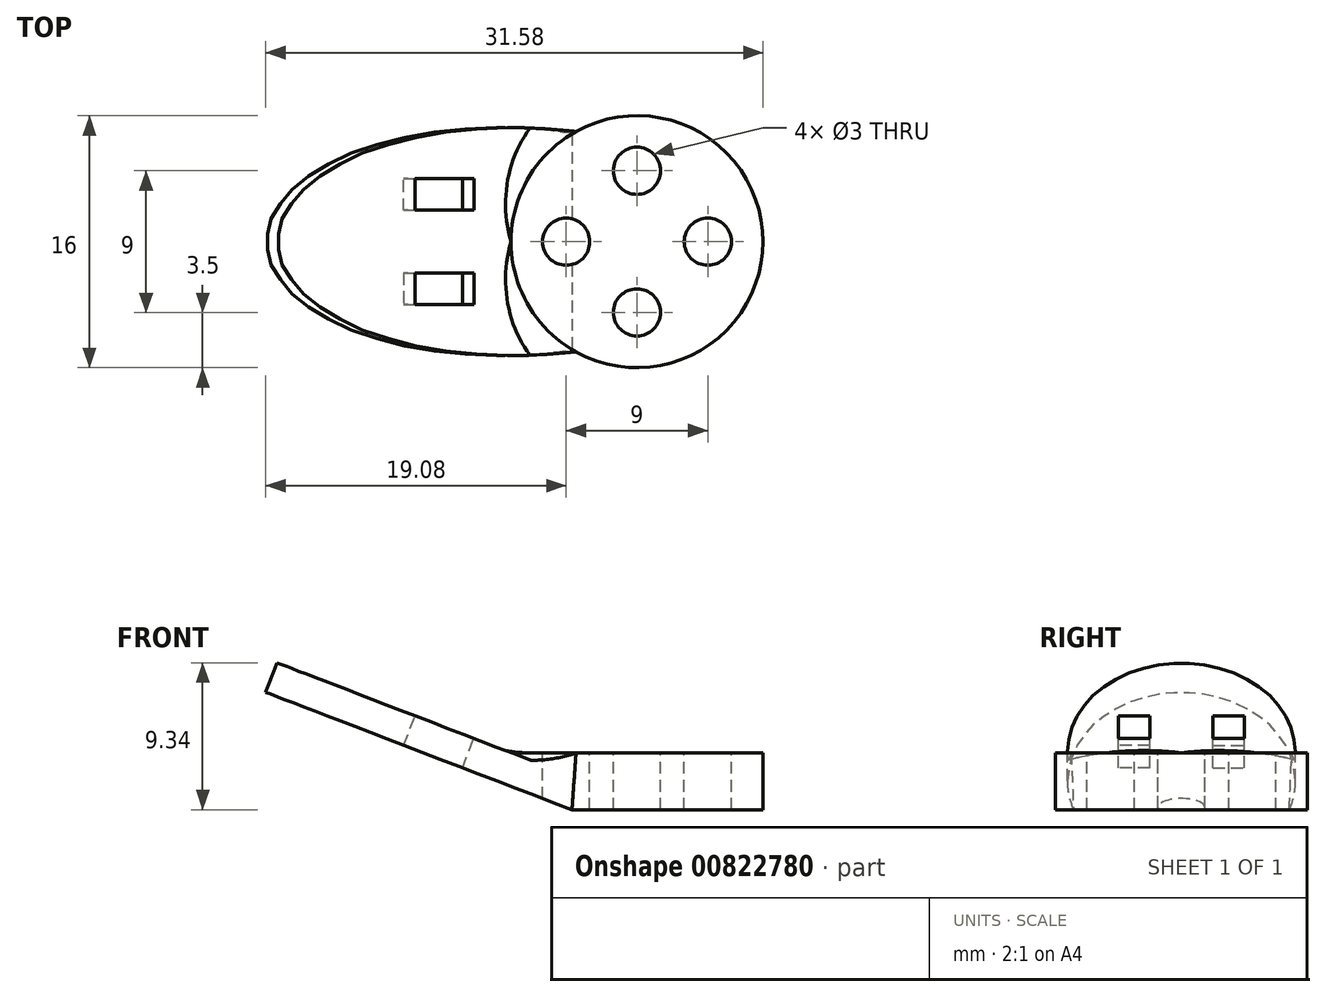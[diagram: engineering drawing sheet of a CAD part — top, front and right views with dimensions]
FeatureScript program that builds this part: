
annotation { "Feature Type Name" : "Feature", "Feature Type Description" : "" }
export const myFeature = defineFeature(function(context is Context, id is Id, definition is map)
    precondition{}
    {
        {
            var Q0;
            Q0=qCreatedBy(makeId("Top.planeOp"),FACE);
            var sketch = newSketch(context, id + "F0", { "sketchPlane" : qUnion([Q0])});
            skCircle(sketch, "E0", {"center": v(0, 0) * mm, "radius": 8 * mm});
            skPoint(sketch, "E1", {"position": v(-8, 0) * mm});
            skSolve(sketch);
        }
        {
            var Q0;
            Q0=qCreatedBy(makeId("Front.planeOp"),FACE);
            var sketch = newSketch(context, id + "F1", { "sketchPlane" : qUnion([Q0])});
            skLineSegment(sketch, "E2", {"start": v(0, 0) * mm, "end": v(6.14, 15.98) * mm});
            skSolve(sketch);
        }
        {
            var Q0;
            Q0=sQuery(id+"F0.wireOp",VERTEX,"E1");
            var Q1;
            Q1=sQuery(id+"F1.wireOp",EDGE,"E2");
            cPlane(context, id + "F2", {"entities" : qUnion([Q0, Q1]), "cplaneType" : CPlaneType.LINE_POINT, "offset" : 25 * mm, "width" : 150 * mm, "height" : 150 * mm});
        }
        {
            var Q0;
            Q0=qCreatedBy(id+"F2.planeOp",FACE);
            var sketch = newSketch(context, id + "F3", { "sketchPlane" : qUnion([Q0])});
            skEllipse(sketch, "E3", {"center": v(-7.69, 0) * mm, "majorRadius": 15.7 * mm, "minorRadius": 7.25 * mm, "majorAxis": v(-1, 0)});
            skSolve(sketch);
        }
        {
            var Q0;
            Q0=makeQuery(id+"F3.imprint","IMPRINT",FACE,{"disambiguationData":[TD([[makeQuery(id+"F3.imprint","IMPRINT",EDGE,{"derivedFrom":sQuery(id+"F3.wireOp",EDGE,"E3")}),1.0]])]});
            extrude(context, id + "F4", {"entities" : qUnion([Q0]), "oppositeDirection" : true, "depth" : 2 * mm, "offsetDistance" : 25 * mm});
        }
        {
            var Q0;
            Q0=makeQuery(id+"F0.imprint","IMPRINT",FACE,{"disambiguationData":[TD([[makeQuery(id+"F0.imprint","IMPRINT",EDGE,{"derivedFrom":sQuery(id+"F0.wireOp",EDGE,"E0")}),1.0]])]});
            var Q1;
            Q1=makeQuery(id+"F4.opExtrude","CAP_FACE",FACE,{"disambiguationData":[OSD([sQuery(id+"F3.wireOp",EDGE,"E3")])],"isStart":false});
            extrude(context, id + "F5", {"entities" : qUnion([Q0]), "operationType" : NewBodyOperationType.ADD, "endBound" : BoundingType.UP_TO_SURFACE, "oppositeDirection" : true, "depth" : 25 * mm, "endBoundEntityFace" : qUnion([Q1]), "offsetDistance" : 25 * mm});
        }
        {
            var Q0;
            Q0=qCreatedBy(makeId("Front.planeOp"),FACE);
            var sketch = newSketch(context, id + "F6", { "sketchPlane" : qUnion([Q0])});
            skLineSegment(sketch, "E4.bottom", {"start": v(-4.13, -3.63) * mm, "end": v(11.59, -3.63) * mm});
            skLineSegment(sketch, "E4.top", {"start": v(-4.13, -13.17) * mm, "end": v(11.59, -13.17) * mm});
            skLineSegment(sketch, "E4.left", {"start": v(-4.13, -3.63) * mm, "end": v(-4.13, -13.17) * mm});
            skLineSegment(sketch, "E4.right", {"start": v(11.59, -3.63) * mm, "end": v(11.59, -13.17) * mm});
            skSolve(sketch);
        }
        {
            var Q0;
            Q0=makeQuery(id+"F6.imprint","IMPRINT",FACE,{"disambiguationData":[TD([[makeQuery(id+"F6.imprint","IMPRINT",EDGE,{"derivedFrom":sQuery(id+"F6.wireOp",EDGE,"E4.bottom")}),-1.0]])]});
            extrude(context, id + "F7", {"entities" : qUnion([Q0]), "operationType" : NewBodyOperationType.REMOVE, "oppositeDirection" : true, "depth" : 25 * mm, "offsetDistance" : 25 * mm, "hasSecondDirection" : true, "secondDirectionOppositeDirection" : false, "secondDirectionDepth" : 25 * mm});
        }
        {
            var Q0;
            Q0=makeQuery(id+"F5.opExtrude","CAP_FACE",FACE,{"disambiguationData":[OSD([sQuery(id+"F0.wireOp",EDGE,"E0")])],"isStart":true});
            var sketch = newSketch(context, id + "F8", { "sketchPlane" : qUnion([Q0])});
            skCircle(sketch, "E5", {"center": v(0, 0) * mm, "radius": 4.5 * mm});
            skPoint(sketch, "E6", {"position": v(-4.5, 0) * mm});
            skPoint(sketch, "E7", {"position": v(0, 4.5) * mm});
            skPoint(sketch, "E8", {"position": v(4.5, 0) * mm});
            skPoint(sketch, "E9", {"position": v(0, -4.5) * mm});
            skSolve(sketch);
        }
        {
            var Q0;
            Q0=sQuery(id+"F8.wireOp",VERTEX,"E7");
            var Q1;
            Q1=sQuery(id+"F8.wireOp",VERTEX,"E6");
            var Q2;
            Q2=sQuery(id+"F8.wireOp",VERTEX,"E8");
            var Q3;
            Q3=sQuery(id+"F8.wireOp",VERTEX,"E9");
            var Q4;
            Q4=makeQuery(id+"F4.opExtrude","SWEPT_BODY",BODY,{"disambiguationData":[OSD([sQuery(id+"F3.wireOp",EDGE,"E3")])]});
            hole(context, id + "F9", {"style" : HoleStyle.SIMPLE, "endStyle" : HoleEndStyle.BLIND, "holeDiameter" : 3 * mm, "majorDiameter" : 5 * mm, "holeDepth" : 25 * mm, "isTappedThrough" : true, "tappedDepth" : 12 * mm, "tapClearance" : 3, "locations" : qUnion([Q0, Q1, Q2, Q3]), "scope" : qUnion([Q4])});
        }
        {
            var Q0;
            Q0=makeQuery(id+"F4.opExtrude","CAP_FACE",FACE,{"disambiguationData":[OSD([sQuery(id+"F3.wireOp",EDGE,"E3")])],"isStart":true});
            var sketch = newSketch(context, id + "F10", { "sketchPlane" : qUnion([Q0])});
            skLineSegment(sketch, "E10", {"start": v(0, 0) * mm, "end": v(-26.8, 0) * mm, "construction": true});
            skLineSegment(sketch, "E11.bottom", {"start": v(-10, -2) * mm, "end": v(-14, -2) * mm});
            skLineSegment(sketch, "E11.top", {"start": v(-10, -4) * mm, "end": v(-14, -4) * mm});
            skLineSegment(sketch, "E11.left", {"start": v(-10, -2) * mm, "end": v(-10, -4) * mm});
            skLineSegment(sketch, "E11.right", {"start": v(-14, -2) * mm, "end": v(-14, -4) * mm});
            skLineSegment(sketch, "E12.MirrorCS", {"start": v(-14, 2) * mm, "end": v(-14, 4) * mm});
            skLineSegment(sketch, "E13.MirrorCS", {"start": v(-10, 2) * mm, "end": v(-10, 4) * mm});
            skLineSegment(sketch, "E14.MirrorCS", {"start": v(-10, 2) * mm, "end": v(-14, 2) * mm});
            skLineSegment(sketch, "E15.MirrorCS", {"start": v(-10, 4) * mm, "end": v(-14, 4) * mm});
            skSolve(sketch);
        }
        {
            var Q0;
            Q0=makeQuery(id+"F10.imprint","IMPRINT",FACE,{"disambiguationData":[TD([[makeQuery(id+"F10.imprint","IMPRINT",EDGE,{"derivedFrom":sQuery(id+"F10.wireOp",EDGE,"E12.MirrorCS")}),-1.0]])]});
            var Q1;
            Q1=makeQuery(id+"F10.imprint","IMPRINT",FACE,{"disambiguationData":[TD([[makeQuery(id+"F10.imprint","IMPRINT",EDGE,{"derivedFrom":sQuery(id+"F10.wireOp",EDGE,"E11.bottom")}),1.0]])]});
            extrude(context, id + "F11", {"entities" : qUnion([Q0, Q1]), "operationType" : NewBodyOperationType.REMOVE, "oppositeDirection" : true, "depth" : 25 * mm, "offsetDistance" : 25 * mm});
        }
        {
            var Q0;
            Q0=makeQuery(id+"F5.boolean.opBoolean","INTERSECT",EDGE,{"disambiguationData":[OD(0.0)],"derivedFrom":[makeQuery(id+"F4.opExtrude","CAP_FACE",FACE,{"disambiguationData":[OSD([sQuery(id+"F3.wireOp",EDGE,"E3")])],"isStart":true}),makeQuery(id+"F5.opExtrude","SWEPT_FACE",FACE,{"disambiguationData":[OSD([sQuery(id+"F0.wireOp",EDGE,"E0")])]})]});
            fillet(context, id + "F12", {"entities" : qUnion([Q0]), "radius" : 2 * mm, "tangentPropagation" : true, "rho" : .1, "crossSection" : FilletCrossSection.CONIC, "allowEdgeOverflow" : false});
        }
    });
